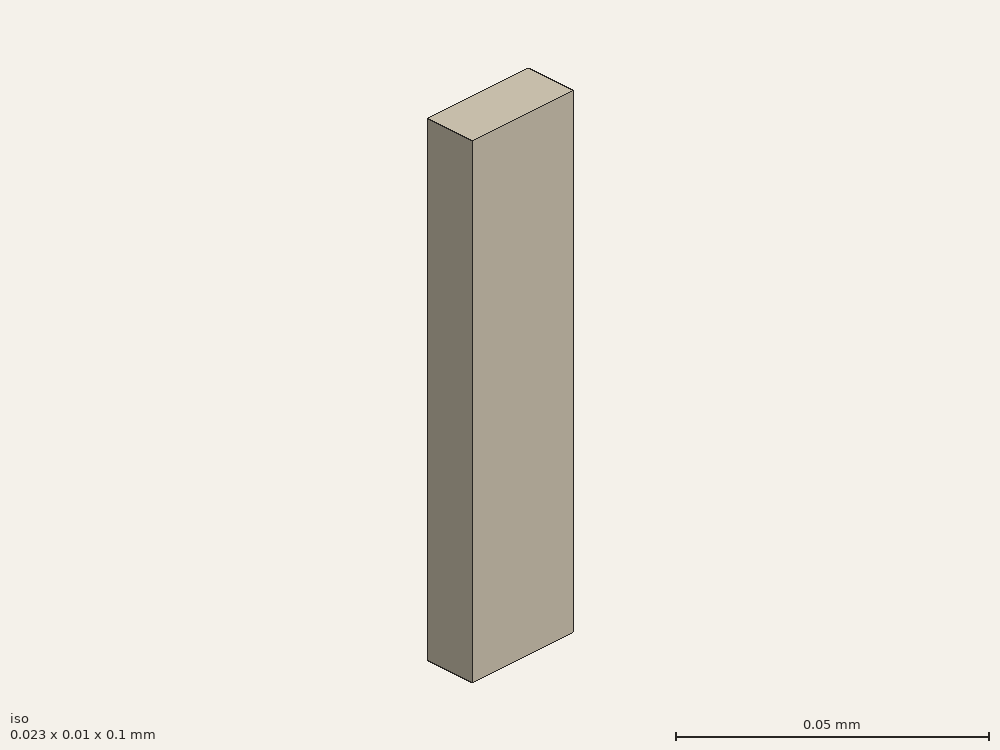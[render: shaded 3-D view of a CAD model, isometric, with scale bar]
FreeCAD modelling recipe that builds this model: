
FCSTD DOCUMENT  (FreeCAD 0.21R33694 (Git))
Label: straight-flipped
License: All rights reserved
LicenseURL: http://en.wikipedia.org/wiki/All_rights_reserved
objects: Part::Part2DObjectPython×5, App::FeaturePython×4, Part::Extrusion×1, Part::FeaturePython×1
note: 7 computed .brp shape members not serialized (recipe doc carries the construction recipe); baked Part::Feature solids carry a one-line shape summary decoded from their .brp

FEATURE [Part::Part2DObjectPython] Rectangle  # Draft 2D object (typed FeaturePython)
  Area = 232.258
  ChamferSize = 0
  Columns = 1
  FilletRadius = 0
  Height = 10.16
  Length = 22.86
  MakeFace = true
  Placement = pos=(-11.43,-5.08,0) rot=(0,0,1;0rad)
  Rows = 1
FEATURE [Part::Extrusion] Extrude
  Base = -> Rectangle
  Dir = (0,0,1)
  DirMode = 2
  FaceMakerClass = Part::FaceMakerBullseye
  LengthFwd = 100
  LengthRev = 0
  Solid = false
  Symmetric = false
FEATURE [Part::FeaturePython] Clone  label="Extrude001"  # Draft clone (typed FeaturePython)
  AttacherType = Attacher::AttachEngine3D
  Fuse = false
  Objects = -> [Extrude]
  Placement = pos=(0,0,0) rot=(1,0,0;3.14159rad)
  Scale = (0.001,0.001,0.001)
FEATURE [Part::Part2DObjectPython] Rectangle001  label="_Pport1"  # Draft 2D object (typed FeaturePython)
  Area = 0.000232258
  ChamferSize = 0
  Columns = 1
  FilletRadius = 0
  Height = 0.01016
  Length = 0.02286
  MakeFace = true
  Placement = pos=(-0.01143,0.00508,-0.1) rot=(1,0,0;3.14159rad)
  Rows = 1
FEATURE [Part::Part2DObjectPython] Line  label="_Pv1"  # Draft 2D object (typed FeaturePython)
  Area = 0
  ChamferSize = 0
  Closed = false
  End = (-1.8e-15,-0.00508,-0.1)
  FilletRadius = 0
  Length = 0.01016
  MakeFace = true
  Placement = pos=(0,0.00508,-0.1) rot=(1,0,0;3.14159rad)
  Points = (2) [(0,0,0),(-1.77605e-15,0.01016,0)]
  Start = (0,0.00508,-0.1)
  Subdivisions = 0
FEATURE [Part::Part2DObjectPython] Rectangle002  label="_Pport2"  # Draft 2D object (typed FeaturePython)
  Area = 0.000232258
  ChamferSize = 0
  Columns = 1
  FilletRadius = 0
  Height = 0.01016
  Length = 0.02286
  MakeFace = true
  Placement = pos=(-0.01143,0.00508,0) rot=(1,0,0;3.14159rad)
  Rows = 1
FEATURE [Part::Part2DObjectPython] Line001  label="_Pv2"  # Draft 2D object (typed FeaturePython)
  Area = 0
  ChamferSize = 0
  Closed = false
  End = (0,-0.00508,0)
  FilletRadius = 0
  Length = 0.01016
  MakeFace = true
  Placement = pos=(0,0.00508,0) rot=(1,0,0;3.14159rad)
  Points = (2) [(0,0,0),(3.1106e-19,0.01016,0)]
  Start = (0,0.00508,0)
  Subdivisions = 0
FEATURE [App::FeaturePython] Text  label="_S1(PV){port1}"  # WARN: FeaturePython — macro-defined, semantics opaque (R4)
  Placement = pos=(0.0413747,-0.017509,0) rot=(0,0,1;0rad)
  Text = .
FEATURE [App::FeaturePython] Text001  label="_S2(PV){port2}"  # WARN: FeaturePython — macro-defined, semantics opaque (R4)
  Placement = pos=(0.0413747,-0.017509,0) rot=(0,0,1;0rad)
  Text = .
FEATURE [App::FeaturePython] Text002  label="_L1(1,voltage){v1}"  # WARN: FeaturePython — macro-defined, semantics opaque (R4)
  Placement = pos=(0.0413747,-0.017509,0) rot=(0,0,1;0rad)
  Text = .
FEATURE [App::FeaturePython] Text003  label="_L2(2,voltage){v2}"  # WARN: FeaturePython — macro-defined, semantics opaque (R4)
  Placement = pos=(0.0413747,-0.017509,0) rot=(0,0,1;0rad)
  Text = .
